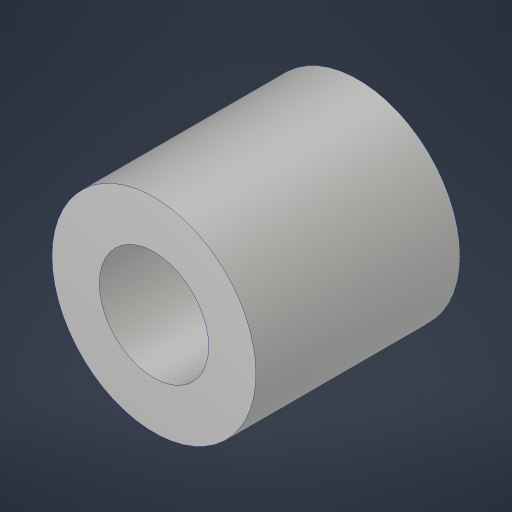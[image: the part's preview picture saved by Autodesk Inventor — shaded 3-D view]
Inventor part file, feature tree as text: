
AUTODESK INVENTOR PART (.ipt)
format: ipt  version: 2023.4 (Build 274418000, 418)  size: 173,568 bytes
history: native  units: in
note: dims shown in document units (in); Inventor stores cm internally (conversion verified against a paired STEP export)
features: extrude x1, hole x1
ambient origin geometry x8: Origin, YZ Plane, XZ Plane, XY Plane, X Axis, Y Axis, Z Axis, Center Point
bodies: Solid1 (feature_tree)
feature tree (2):
  extrude  "Extrusion1"  Depth=0.375in
  hole  "Hole1"  [1 undecoded]
note: 1 required parameter value undecoded (feature->parameter linkage not recoverable at this tier; creation-order binding heuristic only, values carry confidence <= 0.55)
